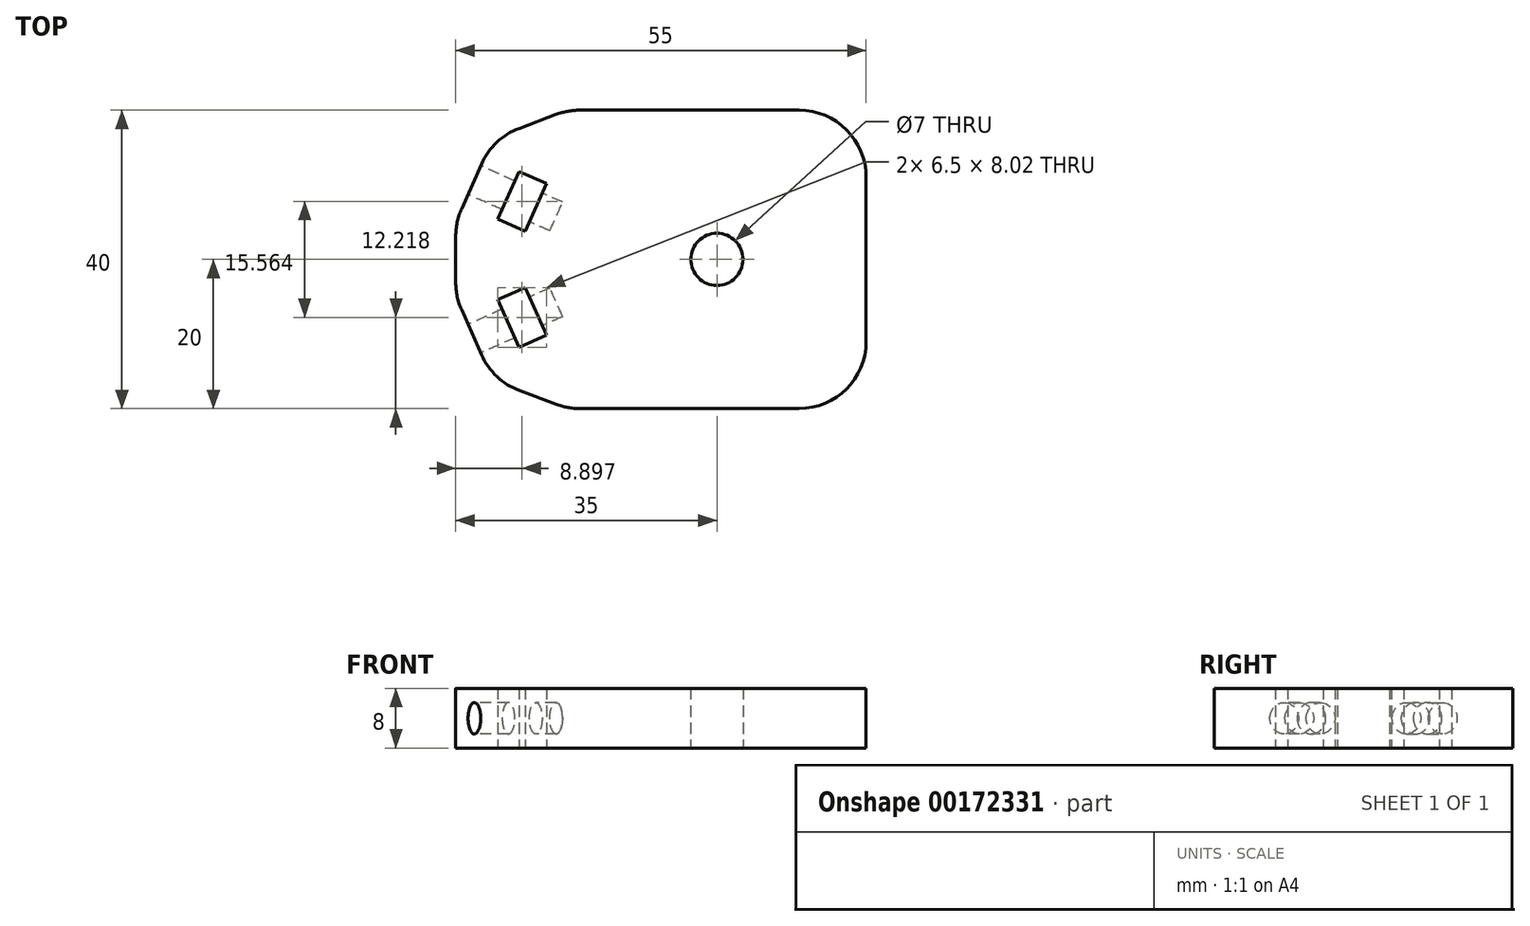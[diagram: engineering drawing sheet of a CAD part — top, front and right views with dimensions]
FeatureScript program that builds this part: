
annotation { "Feature Type Name" : "Feature", "Feature Type Description" : "" }
export const myFeature = defineFeature(function(context is Context, id is Id, definition is map)
    precondition{}
    {
        {
            var Q0;
            Q0=qCreatedBy(makeId("Top.planeOp"),FACE);
            var sketch = newSketch(context, id + "F0", { "sketchPlane" : qUnion([Q0])});
            skLineSegment(sketch, "E0.bottom", {"start": v(20, 20) * mm, "end": v(-20, 20) * mm});
            skLineSegment(sketch, "E0.top", {"start": v(20, -20) * mm, "end": v(-20, -20) * mm});
            skLineSegment(sketch, "E0.left", {"start": v(20, 20) * mm, "end": v(20, -20) * mm});
            skLineSegment(sketch, "E0.right", {"start": v(-20, 20) * mm, "end": v(-20, -20) * mm});
            skPoint(sketch, "E0.middle", {"position": v(0, 0) * mm});
            skLineSegment(sketch, "E1", {"start": v(0, 0) * mm, "end": v(-20, 0) * mm, "construction": true});
            skLineSegment(sketch, "E2", {"start": v(-20, 0) * mm, "end": v(-30, 0) * mm, "construction": true});
            skLineSegment(sketch, "E3", {"start": v(-30, 0) * mm, "end": v(-30, 16.25) * mm});
            skLineSegment(sketch, "E4", {"start": v(-30, 0) * mm, "end": v(-30, -16.25) * mm});
            skLineSegment(sketch, "E5", {"start": v(-30, 0) * mm, "end": v(-35, 0) * mm, "construction": true});
            skLineSegment(sketch, "E6", {"start": v(-30, 16.25) * mm, "end": v(-20, 20) * mm});
            skLineSegment(sketch, "E7", {"start": v(-20, -20) * mm, "end": v(-30, -16.25) * mm});
            skLineSegment(sketch, "E8", {"start": v(-35, 0) * mm, "end": v(-35, -5) * mm});
            skLineSegment(sketch, "E9", {"start": v(-35, 0) * mm, "end": v(-35, 5) * mm});
            skCircle(sketch, "E10", {"center": v(0, 0) * mm, "radius": 3.5 * mm});
            skLineSegment(sketch, "E11", {"start": v(-30, 16.25) * mm, "end": v(-35, 5) * mm});
            skLineSegment(sketch, "E12", {"start": v(-35, -5) * mm, "end": v(-30, -16.25) * mm});
            skLineSegment(sketch, "E13", {"start": v(-32.5, -10.62) * mm, "end": v(-27.93, -8.6) * mm, "construction": true});
            skLineSegment(sketch, "E14", {"start": v(-32.5, 10.62) * mm, "end": v(-27.93, 8.6) * mm, "construction": true});
            skLineSegment(sketch, "E15", {"start": v(-27.93, 8.6) * mm, "end": v(-26.5, 11.8) * mm});
            skLineSegment(sketch, "E16", {"start": v(-26.5, 11.8) * mm, "end": v(-22.85, 10.17) * mm});
            skLineSegment(sketch, "E17", {"start": v(-22.85, 10.17) * mm, "end": v(-25.7, 3.77) * mm});
            skLineSegment(sketch, "E18", {"start": v(-25.7, 3.77) * mm, "end": v(-29.35, 5.4) * mm});
            skLineSegment(sketch, "E19", {"start": v(-27.93, 8.6) * mm, "end": v(-29.35, 5.4) * mm});
            skLineSegment(sketch, "E20", {"start": v(-27.93, -8.6) * mm, "end": v(-29.35, -5.4) * mm});
            skLineSegment(sketch, "E21", {"start": v(-29.35, -5.4) * mm, "end": v(-25.7, -3.77) * mm});
            skLineSegment(sketch, "E22", {"start": v(-25.7, -3.77) * mm, "end": v(-22.85, -10.17) * mm});
            skLineSegment(sketch, "E23", {"start": v(-22.85, -10.17) * mm, "end": v(-26.5, -11.8) * mm});
            skLineSegment(sketch, "E24", {"start": v(-26.5, -11.8) * mm, "end": v(-27.93, -8.6) * mm});
            skSolve(sketch);
        }
        {
            var Q0;
            Q0=makeQuery(id+"F0.imprint","IMPRINT",FACE,{"disambiguationData":[TD([[makeQuery(id+"F0.imprint","IMPRINT",EDGE,{"derivedFrom":sQuery(id+"F0.wireOp",EDGE,"E3")}),1.0]])]});
            var Q1;
            Q1=makeQuery(id+"F0.imprint","IMPRINT",FACE,{"disambiguationData":[TD([[makeQuery(id+"F0.imprint","IMPRINT",EDGE,{"derivedFrom":sQuery(id+"F0.wireOp",EDGE,"E0.right")}),-1.0]])]});
            var Q2;
            Q2=makeQuery(id+"F0.imprint","IMPRINT",FACE,{"disambiguationData":[TD([[makeQuery(id+"F0.imprint","IMPRINT",EDGE,{"derivedFrom":sQuery(id+"F0.wireOp",EDGE,"E0.bottom")}),1.0]])]});
            extrude(context, id + "F1", {"entities" : qUnion([Q0, Q1, Q2]), "depth" : 8 * mm});
        }
        {
            var Q0;
            Q0=makeQuery(id+"F1.opExtrude","SWEPT_FACE",FACE,{"disambiguationData":[OSD([sQuery(id+"F0.wireOp",EDGE,"E11")])]});
            var sketch = newSketch(context, id + "F2", { "sketchPlane" : qUnion([Q0])});
            skCircle(sketch, "E25", {"center": v(3.5, 4) * mm, "radius": 2.1 * mm});
            skPoint(sketch, "E25.centerSnap0", {"position": v(-2.67, 4) * mm});
            skPoint(sketch, "E25.centerSnap1", {"position": v(3.5, 8) * mm});
            skSolve(sketch);
        }
        {
            var Q0;
            Q0 = qSketchRegion(id + "F2", true);
            extrude(context, id + "F3", {"entities" : qUnion([Q0]), "operationType" : NewBodyOperationType.REMOVE, "oppositeDirection" : true, "depth" : 12 * mm});
        }
        {
            var Q0;
            Q0=makeQuery(id+"F1.opExtrude","SWEPT_FACE",FACE,{"disambiguationData":[OSD([sQuery(id+"F0.wireOp",EDGE,"E12")])]});
            var sketch = newSketch(context, id + "F4", { "sketchPlane" : qUnion([Q0])});
            skCircle(sketch, "E26", {"center": v(-3.5, 4) * mm, "radius": 2.1 * mm});
            skPoint(sketch, "E26.centerSnap0", {"position": v(-9.65, 4) * mm});
            skPoint(sketch, "E26.centerSnap1", {"position": v(-3.5, 8) * mm});
            skSolve(sketch);
        }
        {
            var Q0;
            Q0=makeQuery(id+"F4.imprint","IMPRINT",FACE,{"disambiguationData":[TD([[makeQuery(id+"F4.imprint","IMPRINT",EDGE,{"derivedFrom":sQuery(id+"F4.wireOp",EDGE,"E26")}),1.0]])]});
            extrude(context, id + "F5", {"entities" : qUnion([Q0]), "operationType" : NewBodyOperationType.REMOVE, "oppositeDirection" : true, "depth" : 12 * mm});
        }
        {
            var Q0;
            Q0=makeQuery(id+"F1.opExtrude","SWEPT_EDGE",EDGE,{"disambiguationData":[OSD([sQuery(id+"F0.wireOp",EDGE,"E0.top"),sQuery(id+"F0.wireOp",EDGE,"E0.left")])]});
            var Q1;
            Q1=makeQuery(id+"F1.opExtrude","SWEPT_EDGE",EDGE,{"disambiguationData":[OSD([sQuery(id+"F0.wireOp",EDGE,"E0.bottom"),sQuery(id+"F0.wireOp",EDGE,"E0.left")])]});
            var Q2;
            Q2=makeQuery(id+"F1.opExtrude","SWEPT_EDGE",EDGE,{"disambiguationData":[OSD([sQuery(id+"F0.wireOp",EDGE,"E0.top"),sQuery(id+"F0.wireOp",EDGE,"E0.right"),sQuery(id+"F0.wireOp",EDGE,"E7")])]});
            var Q3;
            Q3=makeQuery(id+"F1.opExtrude","SWEPT_EDGE",EDGE,{"disambiguationData":[OSD([sQuery(id+"F0.wireOp",EDGE,"E4"),sQuery(id+"F0.wireOp",EDGE,"E7"),sQuery(id+"F0.wireOp",EDGE,"yKtRZPKS-6oYM-WHJL-Oczw-WfXQsT2mBV9E")])]});
            var Q4;
            Q4=makeQuery(id+"F1.opExtrude","SWEPT_EDGE",EDGE,{"disambiguationData":[OSD([sQuery(id+"F0.wireOp",EDGE,"E8"),sQuery(id+"F0.wireOp",EDGE,"MoDfBmBE-Zycq-enCc-wHg2-CX9js5RwKod5")])]});
            var Q5;
            Q5=makeQuery(id+"F1.opExtrude","SWEPT_EDGE",EDGE,{"disambiguationData":[OSD([sQuery(id+"F0.wireOp",EDGE,"E9"),sQuery(id+"F0.wireOp",EDGE,"hwMoZkL8-HWZg-phh7-HFgU-XUwMWYbgdtiQ")])]});
            var Q6;
            Q6=makeQuery(id+"F1.opExtrude","SWEPT_EDGE",EDGE,{"disambiguationData":[OSD([sQuery(id+"F0.wireOp",EDGE,"E3"),sQuery(id+"F0.wireOp",EDGE,"E6"),sQuery(id+"F0.wireOp",EDGE,"tC4Y1X2g-oi1e-CQev-DTAE-6ImiiB4o7nAa")])]});
            var Q7;
            Q7=makeQuery(id+"F1.opExtrude","SWEPT_EDGE",EDGE,{"disambiguationData":[OSD([sQuery(id+"F0.wireOp",EDGE,"E0.bottom"),sQuery(id+"F0.wireOp",EDGE,"E0.right"),sQuery(id+"F0.wireOp",EDGE,"E6")])]});
            fillet(context, id + "F6", {"entities" : qUnion([Q0, Q1, Q2, Q3, Q4, Q5, Q6, Q7]), "radius" : 9 * mm, "tangentPropagation" : true, "allowEdgeOverflow" : false});
        }
    });
